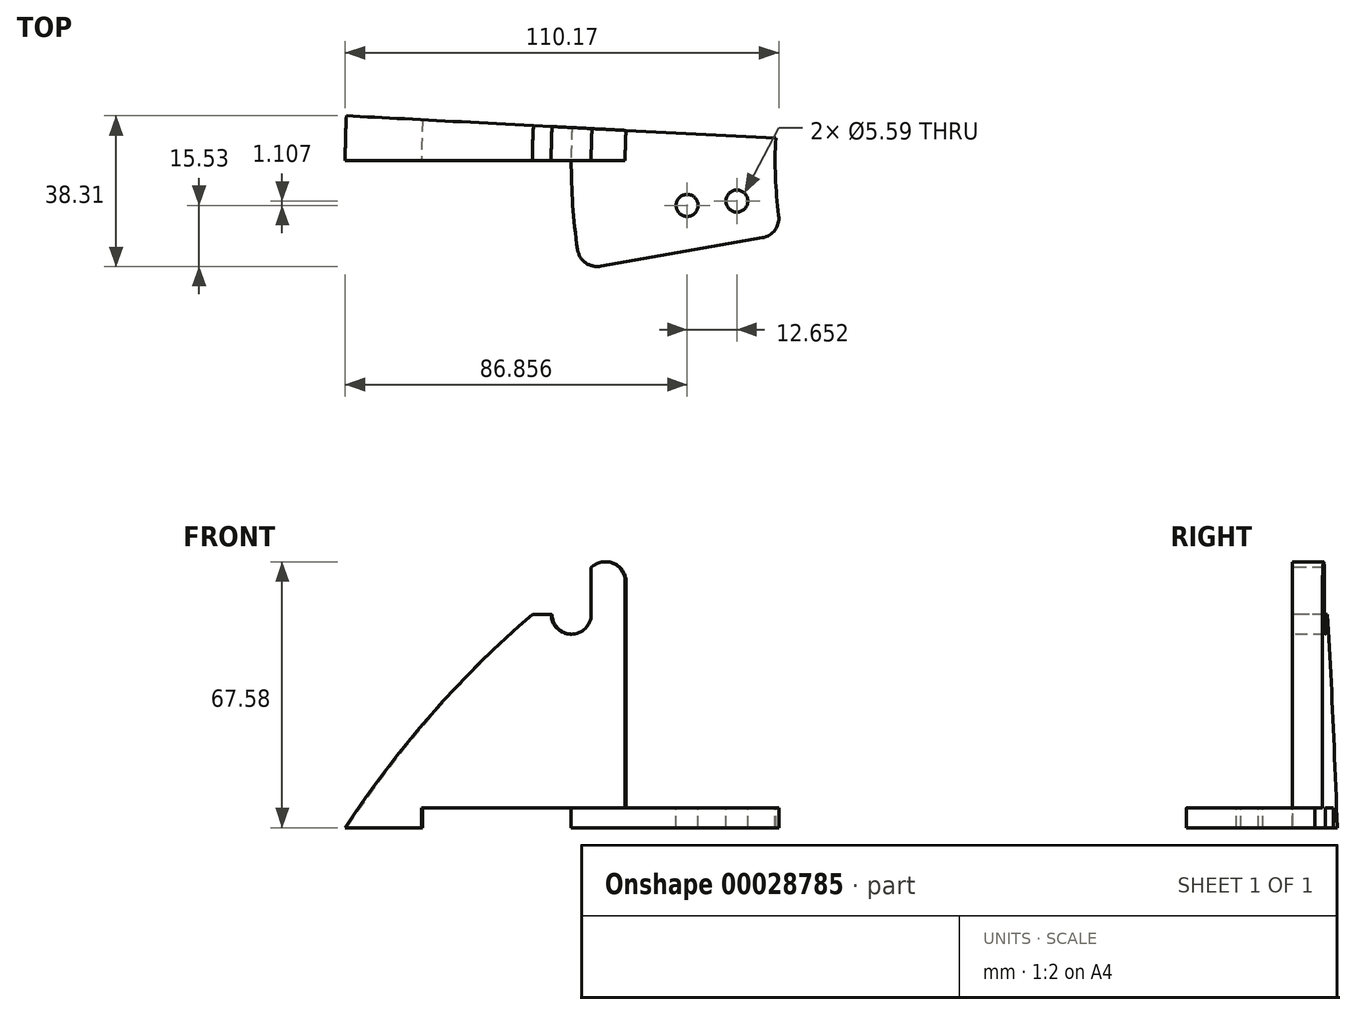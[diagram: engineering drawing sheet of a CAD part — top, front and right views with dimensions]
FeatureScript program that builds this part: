
annotation { "Feature Type Name" : "Feature", "Feature Type Description" : "" }
export const myFeature = defineFeature(function(context is Context, id is Id, definition is map)
    precondition{}
    {
        {
            var Q0;
            Q0=qCreatedBy(makeId("Front.planeOp"),FACE);
            var sketch = newSketch(context, id + "F0", { "sketchPlane" : qUnion([Q0])});
            skArc(sketch, "E0", {"start": v(228.6, 142.24) * mm, "mid": v(228.51, 142.38) * mm, "end": v(228.42, 142.53) * mm});
            skLineSegment(sketch, "E1", {"start": v(0, 269.24) * mm, "end": v(0, -269.24) * mm, "construction": true});
            skLineSegment(sketch, "E2", {"start": v(228.6, 142.53) * mm, "end": v(228.42, 142.53) * mm, "construction": true});
            skLineSegment(sketch, "E3", {"start": v(-279, 76.33) * mm, "end": v(507.36, 76.33) * mm, "construction": true});
            skLineSegment(sketch, "E4", {"start": v(-228.42, 142.53) * mm, "end": v(-228.42, 76.33) * mm, "construction": true});
            skLineSegment(sketch, "E5", {"start": v(-254, 174.53) * mm, "end": v(-254, 8.55) * mm, "construction": true});
            skLineSegment(sketch, "E6", {"start": v(-228.42, 142.53) * mm, "end": v(-254, 76.33) * mm});
            skLineSegment(sketch, "E7", {"start": v(-217.27, 142.53) * mm, "end": v(217.27, 142.53) * mm, "construction": true});
            skArc(sketch, "E8.trimOffspring", {"start": v(254, 54.82) * mm, "mid": v(251.42, 65.63) * mm, "end": v(248.38, 76.33) * mm});
            skArc(sketch, "E9.trimOffspring", {"start": v(0, 259.85) * mm, "mid": v(-123.46, 228.64) * mm, "end": v(-217.27, 142.53) * mm});
            skLineSegment(sketch, "E10", {"start": v(-217.27, 142.53) * mm, "end": v(-242.85, 76.33) * mm});
            skLineSegment(sketch, "E11", {"start": v(-254, 76.33) * mm, "end": v(-242.85, 76.33) * mm});
            skLineSegment(sketch, "E12", {"start": v(0, 269.24) * mm, "end": v(0, 259.85) * mm});
            skPoint(sketch, "E13.end.orphan", {"position": v(243.42, 76.33) * mm});
            skPoint(sketch, "E14.orphan", {"position": v(232.09, 76.33) * mm});
            skArc(sketch, "E15.trimOffspring", {"start": v(0, 269.24) * mm, "mid": v(-130.6, 235.44) * mm, "end": v(-228.42, 142.53) * mm});
            skLineSegment(sketch, "E16.trimOffspring", {"start": v(0, 142.53) * mm, "end": v(-228.42, 142.53) * mm, "construction": true});
            skLineSegment(sketch, "E17", {"start": v(0, 259.85) * mm, "end": v(-183.52, 76.33) * mm, "construction": true});
            skLineSegment(sketch, "E18", {"start": v(-217.27, 142.53) * mm, "end": v(-217.27, 266.7) * mm, "construction": true});
            skLineSegment(sketch, "E19", {"start": v(-146.15, 142.53) * mm, "end": v(-146.15, 289.46) * mm, "construction": true});
            skLineSegment(sketch, "E20", {"start": v(-252.15, 215.8) * mm, "end": v(47.32, 215.8) * mm, "construction": true});
            skLineSegment(sketch, "E21", {"start": v(-146.15, 142.53) * mm, "end": v(-146.15, 214.85) * mm});
            skLineSegment(sketch, "E22", {"start": v(-159.87, 142.53) * mm, "end": v(-159.87, 250.26) * mm, "construction": true});
            skLineSegment(sketch, "E23", {"start": v(-244.24, 196.78) * mm, "end": v(-117.26, 196.78) * mm, "construction": true});
            skCircle(sketch, "E24", {"center": v(-159.87, 196.78) * mm, "radius": 5.08 * mm});
            skLineSegment(sketch, "E25", {"start": v(-154.79, 196.78) * mm, "end": v(-154.79, 208.71) * mm});
            skLineSegment(sketch, "E26", {"start": v(-164.95, 196.78) * mm, "end": v(-169.7, 196.78) * mm});
            skLineSegment(sketch, "E27", {"start": v(-228.42, 142.53) * mm, "end": v(-146.15, 142.53) * mm});
            skLineSegment(sketch, "E28", {"start": v(-146.15, 142.53) * mm, "end": v(-146.15, 226.12) * mm});
            skLineSegment(sketch, "E29.bottom", {"start": v(-159.87, 142.53) * mm, "end": v(-197.88, 142.53) * mm});
            skLineSegment(sketch, "E29.top", {"start": v(-159.87, 147.6) * mm, "end": v(-197.88, 147.6) * mm});
            skLineSegment(sketch, "E29.left", {"start": v(-159.87, 142.53) * mm, "end": v(-159.87, 147.6) * mm});
            skLineSegment(sketch, "E29.right", {"start": v(-197.88, 142.53) * mm, "end": v(-197.88, 147.6) * mm});
            skLineSegment(sketch, "E30", {"start": v(-217.27, 142.53) * mm, "end": v(-120.38, 258) * mm, "construction": true});
            skLineSegment(sketch, "E31", {"start": v(-108.05, 119.31) * mm, "end": v(-108.05, 234.69) * mm, "construction": true});
            skLineSegment(sketch, "E32.bottom", {"start": v(-108.05, 142.53) * mm, "end": v(-159.87, 142.53) * mm});
            skLineSegment(sketch, "E32.top", {"start": v(-108.05, 147.6) * mm, "end": v(-159.87, 147.6) * mm});
            skLineSegment(sketch, "E32.left", {"start": v(-108.05, 142.53) * mm, "end": v(-108.05, 147.6) * mm});
            skLineSegment(sketch, "E33.bottom", {"start": v(-108.05, 147.6) * mm, "end": v(-146.15, 147.6) * mm});
            skLineSegment(sketch, "E33.top", {"start": v(-108.05, 158.4) * mm, "end": v(-146.15, 158.4) * mm});
            skLineSegment(sketch, "E33.left", {"start": v(-108.05, 147.6) * mm, "end": v(-108.05, 158.4) * mm});
            skLineSegment(sketch, "E33.right", {"start": v(-146.15, 147.6) * mm, "end": v(-146.15, 158.4) * mm});
            skSolve(sketch);
        }
        {
            var Q0;
            {var subQ0=sQuery(id+"F0.wireOp",EDGE,"E25");Q0=makeQuery(id+"F0.imprint","IMPRINT",FACE,{"disambiguationData":[TD([[makeQuery(id+"F0.imprint","IMPRINT",EDGE,{"derivedFrom":subQ0}),-1.0]])]});}
            var Q1;
            Q1=makeQuery(id+"F0.imprint","IMPRINT",FACE,{"disambiguationData":[TD([[makeQuery(id+"F0.imprint","IMPRINT",EDGE,{"derivedFrom":sQuery(id+"F0.wireOp",EDGE,"E29.bottom")}),-1.0]])]});
            var Q2;
            Q2=makeQuery(id+"F0.imprint","IMPRINT",FACE,{"disambiguationData":[TD([[makeQuery(id+"F0.imprint","IMPRINT",EDGE,{"derivedFrom":sQuery(id+"F0.wireOp",EDGE,"E33.bottom")}),-1.0]])]});
            var Q3;
            Q3=sQuery(id+"F0.wireOp",EDGE,"E1");
            revolve(context, id + "F1", {"entities" : qUnion([Q0, Q1, Q2]), "axis" : qUnion([Q3]), "revolveType" : RevolveType.ONE_DIRECTION, "angle" : 3 * degree});
        }
        {
            var Q0;
            {var subQ5=sQuery(id+"F0.wireOp",EDGE,"E32.left");Q0=makeQuery(id+"F0.imprint","IMPRINT",FACE,{"disambiguationData":[TD([[makeQuery(id+"F0.imprint","IMPRINT",EDGE,{"derivedFrom":subQ5}),1.0]])]});}
            var Q1;
            {var subQ5=sQuery(id+"F0.wireOp",EDGE,"E29.left");Q1=makeQuery(id+"F0.imprint","IMPRINT",FACE,{"disambiguationData":[TD([[makeQuery(id+"F0.imprint","IMPRINT",EDGE,{"derivedFrom":subQ5}),-1.0]])]});}
            var Q2;
            Q2=sQuery(id+"F0.wireOp",EDGE,"E1");
            revolve(context, id + "F2", {"operationType" : NewBodyOperationType.ADD, "entities" : qUnion([Q0, Q1]), "axis" : qUnion([Q2]), "revolveType" : RevolveType.TWO_DIRECTIONS, "angle" : 3 * degree, "angleBack" : 350 * degree});
        }
        {
            var Q0;
            Q0=makeQuery(id+"F2.opRevolve","SWEPT_FACE",FACE,{"disambiguationData":[OSD([sQuery(id+"F0.wireOp",EDGE,"E32.top"),sQuery(id+"F0.wireOp",EDGE,"E33.bottom")])]});
            var sketch = newSketch(context, id + "F3", { "sketchPlane" : qUnion([Q0])});
            skLineSegment(sketch, "E34", {"start": v(-159.26, -13.93) * mm, "end": v(-107.64, -9.42) * mm, "construction": true});
            skCircle(sketch, "E35", {"center": v(-130.41, -11.4) * mm, "radius": 2.8 * mm});
            skCircle(sketch, "E36", {"center": v(-117.76, -10.3) * mm, "radius": 2.8 * mm});
            skSolve(sketch);
        }
        {
            var Q0;
            Q0=makeQuery(id+"F3.imprint","IMPRINT",FACE,{"disambiguationData":[TD([[makeQuery(id+"F3.imprint","IMPRINT",EDGE,{"derivedFrom":sQuery(id+"F3.wireOp",EDGE,"E35")}),1.0]])]});
            var Q1;
            Q1=makeQuery(id+"F3.imprint","IMPRINT",FACE,{"disambiguationData":[TD([[makeQuery(id+"F3.imprint","IMPRINT",EDGE,{"derivedFrom":sQuery(id+"F3.wireOp",EDGE,"E36")}),1.0]])]});
            extrude(context, id + "F4", {"entities" : qUnion([Q0, Q1]), "operationType" : NewBodyOperationType.REMOVE, "oppositeDirection" : true, "depth" : 25.4 * mm});
        }
        {
            var Q0;
            Q0=makeQuery(id+"F1.opRevolve","SWEPT_EDGE",EDGE,{"disambiguationData":[OSD([sQuery(id+"F0.wireOp",EDGE,"E33.top"),sQuery(id+"F0.wireOp",EDGE,"E33.left")])]});
            var Q1;
            Q1=makeQuery(id+"F1.opRevolve","SWEPT_EDGE",EDGE,{"disambiguationData":[OSD([sQuery(id+"F0.wireOp",EDGE,"E28"),sQuery(id+"F0.wireOp",EDGE,"E33.top"),sQuery(id+"F0.wireOp",EDGE,"E33.right")])]});
            var Q2;
            Q2=makeQuery(id+"F2.opRevolve","CAP_EDGE",EDGE,{"disambiguationData":[OSD([sQuery(id+"F0.wireOp",EDGE,"E32.left")])],"isStart":true});
            var Q3;
            Q3=makeQuery(id+"F2.opRevolve","CAP_EDGE",EDGE,{"disambiguationData":[OSD([sQuery(id+"F0.wireOp",EDGE,"E29.left")])],"isStart":true});
            fillet(context, id + "F5", {"entities" : qUnion([Q0, Q1, Q2, Q3]), "radius" : 5.08 * mm, "tangentPropagation" : true, "allowEdgeOverflow" : false});
        }
    });
